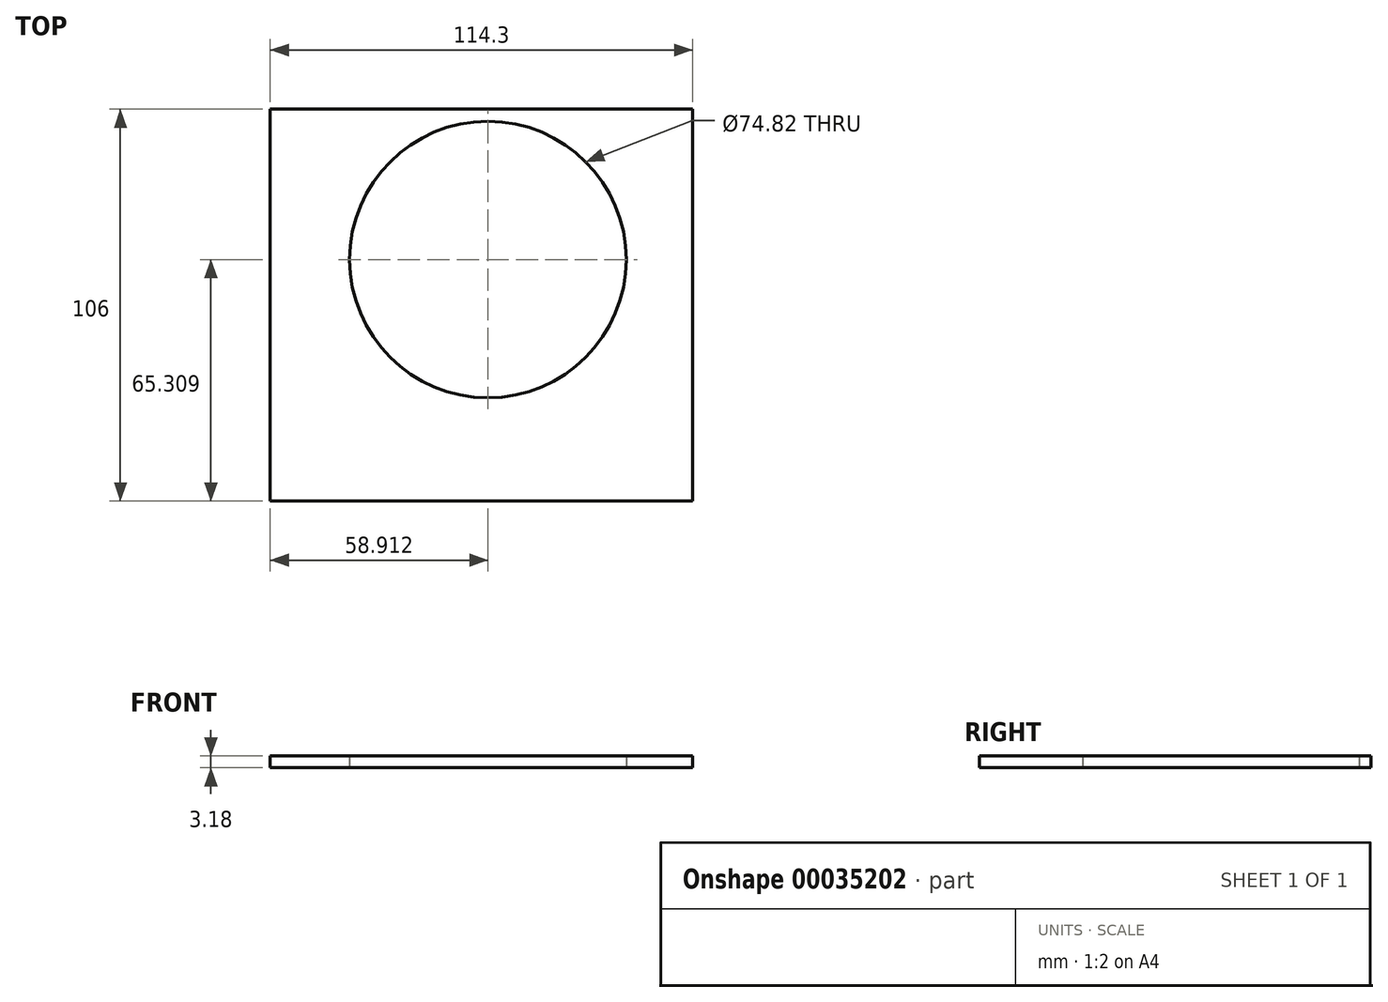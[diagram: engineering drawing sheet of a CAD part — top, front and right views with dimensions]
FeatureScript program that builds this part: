
annotation { "Feature Type Name" : "Feature", "Feature Type Description" : "" }
export const myFeature = defineFeature(function(context is Context, id is Id, definition is map)
    precondition{}
    {
        {
            var Q0;
            Q0=qCreatedBy(makeId("Top.planeOp"),FACE);
            var sketch = newSketch(context, id + "F0", { "sketchPlane" : qUnion([Q0])});
            skLineSegment(sketch, "E0.bottom", {"start": v(-61.5, 55.2) * mm, "end": v(52.8, 55.2) * mm});
            skLineSegment(sketch, "E0.top", {"start": v(-61.5, -50.8) * mm, "end": v(52.8, -50.8) * mm});
            skLineSegment(sketch, "E0.left", {"start": v(-61.5, 55.2) * mm, "end": v(-61.5, -50.8) * mm});
            skLineSegment(sketch, "E0.right", {"start": v(52.8, 55.2) * mm, "end": v(52.8, -50.8) * mm});
            skCircle(sketch, "E1", {"center": v(-2.59, 14.5) * mm, "radius": 37.4 * mm});
            skSolve(sketch);
        }
        {
            var Q0;
            Q0=makeQuery(id+"F0.imprint","IMPRINT",FACE,{"disambiguationData":[TD([[makeQuery(id+"F0.imprint","IMPRINT",EDGE,{"derivedFrom":sQuery(id+"F0.wireOp",EDGE,"E0.bottom")}),-1.0]])]});
            extrude(context, id + "F1", {"entities" : qUnion([Q0]), "depth" : 3.18 * mm});
        }
    });
